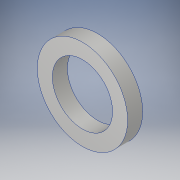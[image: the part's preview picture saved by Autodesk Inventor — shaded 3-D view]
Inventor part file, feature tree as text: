
AUTODESK INVENTOR PART (.ipt)
format: ipt  version: 2017 (Build 210142000, 142)  size: 101,376 bytes
history: native  units: in
note: dims shown in document units (in); Inventor stores cm internally (conversion verified against a paired STEP export)
features: extrude x1, sketch x1
ambient origin geometry x8: Origin, YZ Plane, XZ Plane, XY Plane, X Axis, Y Axis, Z Axis, Center Point
bodies: Solid1 (feature_tree)
feature tree (2):
  extrude  "Extrusion1"  Depth=0.125in
  sketch  "Sketch1"  dims[d0=0.75in d1=0.5in d2=0.125in d3=0.0in]
